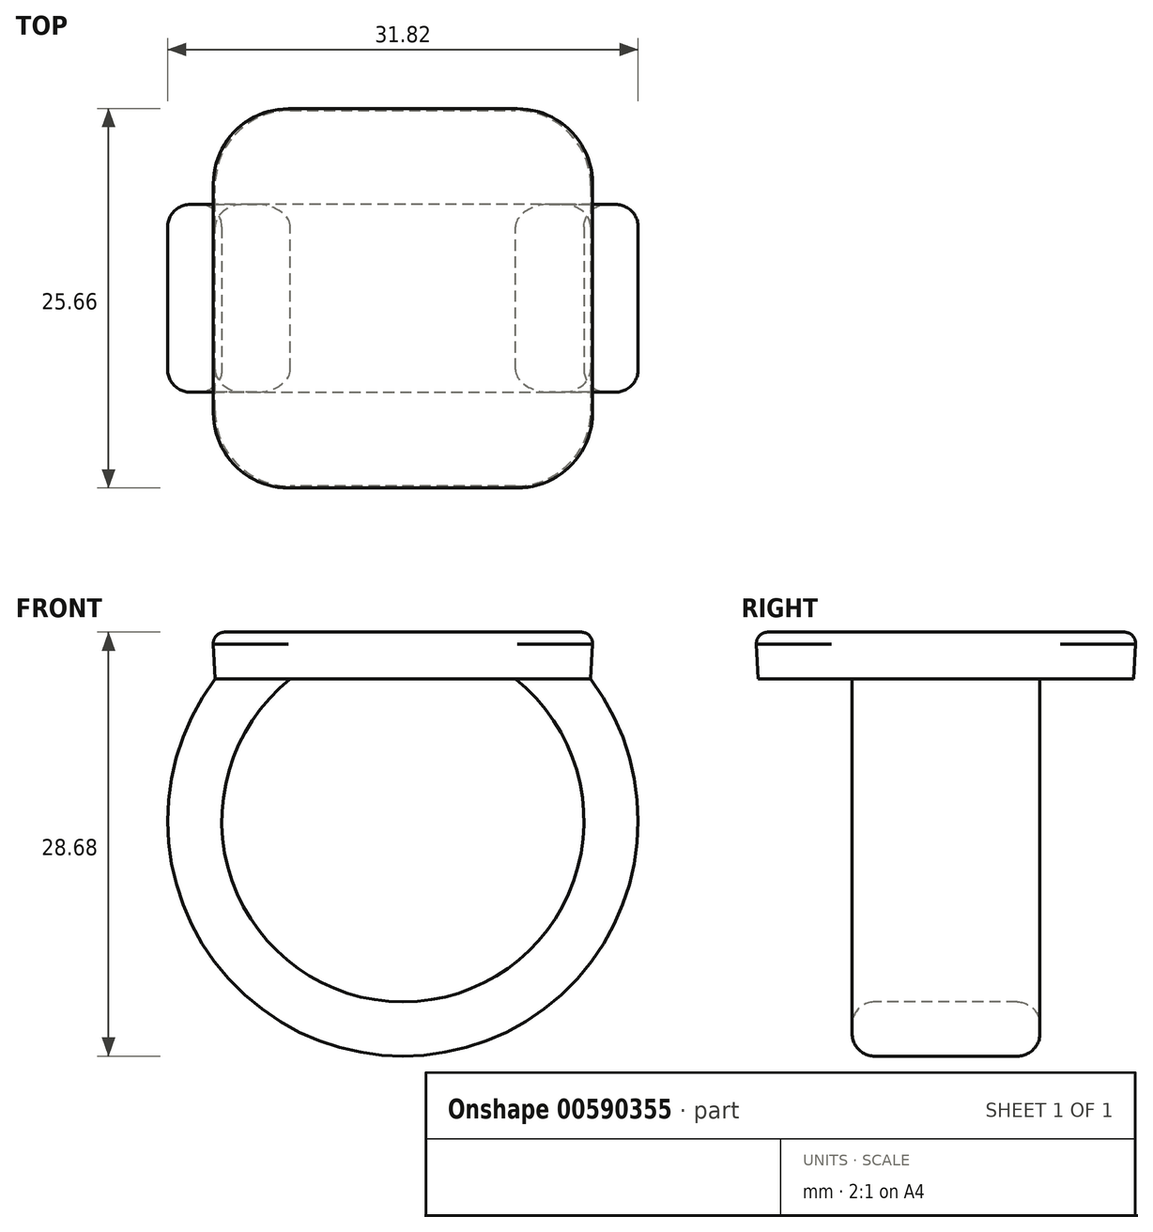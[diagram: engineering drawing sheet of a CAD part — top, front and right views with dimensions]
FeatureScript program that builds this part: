
annotation { "Feature Type Name" : "Feature", "Feature Type Description" : "" }
export const myFeature = defineFeature(function(context is Context, id is Id, definition is map)
    precondition{}
    {
        {
            var Q0;
            Q0=qCreatedBy(makeId("Top.planeOp"),FACE);
            var sketch = newSketch(context, id + "F0", { "sketchPlane" : qUnion([Q0])});
            skLineSegment(sketch, "E0.bottom", {"start": v(-12.7, 12.7) * mm, "end": v(12.7, 12.7) * mm});
            skLineSegment(sketch, "E0.top", {"start": v(-12.7, -12.7) * mm, "end": v(12.7, -12.7) * mm});
            skLineSegment(sketch, "E0.left", {"start": v(-12.7, 12.7) * mm, "end": v(-12.7, -12.7) * mm});
            skLineSegment(sketch, "E0.right", {"start": v(12.7, 12.7) * mm, "end": v(12.7, -12.7) * mm});
            skPoint(sketch, "E0.middle", {"position": v(0, 0) * mm});
            skSolve(sketch);
        }
        {
            var Q0;
            Q0 = qSketchRegion(id + "F0", true);
            extrude(context, id + "F1", {"entities" : qUnion([Q0]), "depth" : 3.17 * mm, "offsetDistance" : 25.4 * mm, "hasDraft" : true, "draftAngle" : 3 * degree});
        }
        {
            var Q0;
            Q0=qCreatedBy(makeId("Front.planeOp"),FACE);
            var sketch = newSketch(context, id + "F2", { "sketchPlane" : qUnion([Q0])});
            skArc(sketch, "E1", {"start": v(-10.16, 0) * mm, "mid": v(0, -23.56) * mm, "end": v(10.16, 0) * mm});
            skSolve(sketch);
        }
        {
            var Q0;
            Q0=makeQuery(id+"F1.opExtrude","CAP_FACE",FACE,{"disambiguationData":[OSD([sQuery(id+"F0.wireOp",EDGE,"E0.bottom"),sQuery(id+"F0.wireOp",EDGE,"E0.top"),sQuery(id+"F0.wireOp",EDGE,"E0.left"),sQuery(id+"F0.wireOp",EDGE,"E0.right")])],"isStart":true});
            var sketch = newSketch(context, id + "F3", { "sketchPlane" : qUnion([Q0])});
            skLineSegment(sketch, "E2.bottom", {"start": v(-7.62, 6.35) * mm, "end": v(-12.7, 6.35) * mm});
            skLineSegment(sketch, "E2.top", {"start": v(-7.62, -6.35) * mm, "end": v(-12.7, -6.35) * mm});
            skLineSegment(sketch, "E2.left", {"start": v(-7.62, 6.35) * mm, "end": v(-7.62, -6.35) * mm});
            skLineSegment(sketch, "E2.right", {"start": v(-12.7, 6.35) * mm, "end": v(-12.7, -6.35) * mm});
            skPoint(sketch, "E2.middle", {"position": v(-10.16, 0) * mm});
            skSolve(sketch);
        }
        {
            var Q0;
            Q0 = qSketchRegion(id + "F3", true);
            var Q1;
            Q1 = qConstructionFilter(qBodyType(qCreatedBy(id + "F2" ,EDGE), BodyType.WIRE), ConstructionObject.NO);
            sweep(context, id + "F4", {"operationType" : NewBodyOperationType.ADD, "profiles" : qUnion([Q0]), "path" : qUnion([Q1])});
        }
        {
            var Q0;
            Q0=qCreatedBy(makeId("Front.planeOp"),FACE);
            var sketch = newSketch(context, id + "F5", { "sketchPlane" : qUnion([Q0])});
            skLineSegment(sketch, "E3.0", {"start": v(7.62, 0) * mm, "end": v(10.16, 0) * mm});
            skArc(sketch, "E3.1", {"start": v(10.01, -2.54) * mm, "mid": v(8.9, -1.18) * mm, "end": v(7.62, 0) * mm});
            skLineSegment(sketch, "E3.2", {"start": v(10.01, -2.54) * mm, "end": v(10.16, 0) * mm});
            skPoint(sketch, "E4.orphan", {"position": v(-7.62, 0) * mm});
            skPoint(sketch, "E5.orphan", {"position": v(-12.7, 0) * mm});
            skPoint(sketch, "E6.orphan", {"position": v(12.7, 0) * mm});
            skSolve(sketch);
        }
        {
            var Q0;
            Q0=makeQuery(id+"F5.imprint","IMPRINT",FACE,{"disambiguationData":[TD([[makeQuery(id+"F5.imprint","IMPRINT",EDGE,{"derivedFrom":sQuery(id+"F5.wireOp",EDGE,"E3.0")}),-1.0]])]});
            var Q1;
            Q1=makeQuery(id+"F4.opSweep","SWEPT_FACE",FACE,{"disambiguationData":[OSD([sQuery(id+"F2.wireOp",EDGE,"E1"),sQuery(id+"F3.wireOp",EDGE,"E2.bottom")])]});
            var Q2;
            Q2=makeQuery(id+"F4.opSweep","SWEPT_FACE",FACE,{"disambiguationData":[OSD([sQuery(id+"F2.wireOp",EDGE,"E1"),sQuery(id+"F3.wireOp",EDGE,"E2.top")])]});
            extrude(context, id + "F6", {"entities" : qUnion([Q0]), "operationType" : NewBodyOperationType.ADD, "endBound" : BoundingType.UP_TO_SURFACE, "depth" : 25.4 * mm, "endBoundEntityFace" : qUnion([Q1]), "offsetDistance" : 25.4 * mm, "hasSecondDirection" : true, "secondDirectionBound" : SecondDirectionBoundingType.UP_TO_SURFACE, "secondDirectionOppositeDirection" : true, "secondDirectionDepth" : 25.4 * mm, "secondDirectionBoundEntityFace" : qUnion([Q2])});
        }
        {
            var Q0;
            Q0=makeQuery(id+"F1.opExtrude","SWEPT_EDGE",EDGE,{"disambiguationData":[OSD([sQuery(id+"F0.wireOp",EDGE,"E0.top"),sQuery(id+"F0.wireOp",EDGE,"E0.left")])]});
            var Q1;
            Q1=makeQuery(id+"F1.opExtrude","SWEPT_EDGE",EDGE,{"disambiguationData":[OSD([sQuery(id+"F0.wireOp",EDGE,"E0.bottom"),sQuery(id+"F0.wireOp",EDGE,"E0.left")])]});
            var Q2;
            Q2=makeQuery(id+"F1.opExtrude","SWEPT_EDGE",EDGE,{"disambiguationData":[OSD([sQuery(id+"F0.wireOp",EDGE,"E0.bottom"),sQuery(id+"F0.wireOp",EDGE,"E0.right")])]});
            var Q3;
            Q3=makeQuery(id+"F1.opExtrude","SWEPT_EDGE",EDGE,{"disambiguationData":[OSD([sQuery(id+"F0.wireOp",EDGE,"E0.top"),sQuery(id+"F0.wireOp",EDGE,"E0.right")])]});
            fillet(context, id + "F7", {"entities" : qUnion([Q0, Q1, Q2, Q3]), "radius" : 5.08 * mm, "tangentPropagation" : true, "allowEdgeOverflow" : false});
        }
        {
            var Q0;
            Q0=makeQuery(id+"F4.opSweep","SWEPT_EDGE",EDGE,{"disambiguationData":[OSD([sQuery(id+"F0.wireOp",EDGE,"E0.left"),sQuery(id+"F2.wireOp",EDGE,"E1"),sQuery(id+"F3.wireOp",EDGE,"E2.bottom"),sQuery(id+"F3.wireOp",EDGE,"E2.right")])]});
            var Q1;
            {var subQ0=sQuery(id+"F3.wireOp",EDGE,"E2.bottom");var subQ1=sQuery(id+"F2.wireOp",EDGE,"E1");Q1=makeQuery(id+"F6.boolean.opBoolean","MERGE",EDGE,{"derivedFrom":[makeQuery(id+"F4.opSweep","SWEPT_EDGE",EDGE,{"disambiguationData":[OSD([subQ1,subQ0,sQuery(id+"F3.wireOp",EDGE,"E2.left")])]}),makeQuery(id+"F6.opExtrude","TWEAK_EDGE",EDGE,{"derivedFrom":[makeQuery(id+"F4.opSweep","SWEPT_FACE",FACE,{"disambiguationData":[OSD([subQ1,subQ0])]}),makeQuery(id+"F5.imprint","IMPRINT",EDGE,{"derivedFrom":sQuery(id+"F5.wireOp",EDGE,"E3.1")})]})]});}
            var Q2;
            {var subQ0=sQuery(id+"F3.wireOp",EDGE,"E2.top");var subQ1=sQuery(id+"F2.wireOp",EDGE,"E1");Q2=makeQuery(id+"F6.boolean.opBoolean","MERGE",EDGE,{"derivedFrom":[makeQuery(id+"F4.opSweep","SWEPT_EDGE",EDGE,{"disambiguationData":[OSD([subQ1,subQ0,sQuery(id+"F3.wireOp",EDGE,"E2.left")])]}),makeQuery(id+"F6.opExtrude","TWEAK_EDGE",EDGE,{"derivedFrom":[makeQuery(id+"F4.opSweep","SWEPT_FACE",FACE,{"disambiguationData":[OSD([subQ1,subQ0])]}),makeQuery(id+"F5.imprint","IMPRINT",EDGE,{"derivedFrom":sQuery(id+"F5.wireOp",EDGE,"E3.1")})]})]});}
            var Q3;
            Q3=makeQuery(id+"F4.opSweep","SWEPT_EDGE",EDGE,{"disambiguationData":[OSD([sQuery(id+"F0.wireOp",EDGE,"E0.left"),sQuery(id+"F2.wireOp",EDGE,"E1"),sQuery(id+"F3.wireOp",EDGE,"E2.top"),sQuery(id+"F3.wireOp",EDGE,"E2.right")])]});
            fillet(context, id + "F8", {"entities" : qUnion([Q0, Q1, Q2, Q3]), "radius" : 1.52 * mm, "tangentPropagation" : true, "allowEdgeOverflow" : false});
        }
        {
            var Q0;
            Q0=makeQuery(id+"F1.opExtrude","CAP_FACE",FACE,{"disambiguationData":[OSD([sQuery(id+"F0.wireOp",EDGE,"E0.bottom"),sQuery(id+"F0.wireOp",EDGE,"E0.top"),sQuery(id+"F0.wireOp",EDGE,"E0.left"),sQuery(id+"F0.wireOp",EDGE,"E0.right")])],"isStart":false});
            fillet(context, id + "F9", {"entities" : qUnion([Q0]), "radius" : 0.76 * mm, "tangentPropagation" : true, "allowEdgeOverflow" : false});
        }
    });
